# Revit family: Table-Teknion-ATVC_Audience_Video_Conference_Table-R2023
name_source: partatom
category: Furniture
units: mm (PartAtom-declared; Revit-internal decimal feet)

## family parameters
Always vertical = Yes
Cut with Voids When Loaded = No
Enable Cutting in Views = No
OmniClass Number = 23.40.20.00
OmniClass Title = General Furniture and Specialties
Render Appearance Source = Family Geometry
Room Calculation Point = No
Shared = Yes
Work Plane-Based = No

## types (4) — shared parameters
Assembly Code = E2020200
Manufacturer = Teknion
Manufacturer Fax = 416.661.4586
Part Number = ATVC
Product Documentation Link = https://www.teknion.com
Product Line = Meeting & Audience Boardroom Tables
Product Page URL = https://www.teknion.com
Series = Tables & Collaborative Spaces
Sustainability Data = https://www.teknion.com
URL = www.teknion.com
Unit Weight URL = http://www.teknion.com
Warranty = http://www.teknion.com
zero-valued in all types: Default Elevation

## per-type parameters (varying)
| type | Depth | Description | Model | Pedestal Base | Stretch Legs |
| Pedestal Base, 54" Depth | 54 " | Audience Video Conference Table,Pedestal Base, 54" Depth | ATVCD54___ | Yes | No |
| Pedestal Base, 60" Depth | 58.5 " | Audience Video Conference Table,Pedestal Base, 60" Depth | ATVCD60___ | Yes | No |
| Stretch Legs, 54" Depth | 54 " | Audience Video Conference Table,Stretch Legs, 54" Depth | ATVCS54___ | No | Yes |
| Stretch Legs, 60" Depth | 58.5 " | Audience Video Conference Table,Stretch Legs, 60" Depth | ATVCS60___ | No | Yes |

## geometry (parser evidence)
native form markers: Sweep x11
no freeform markers — native parametric forms only
